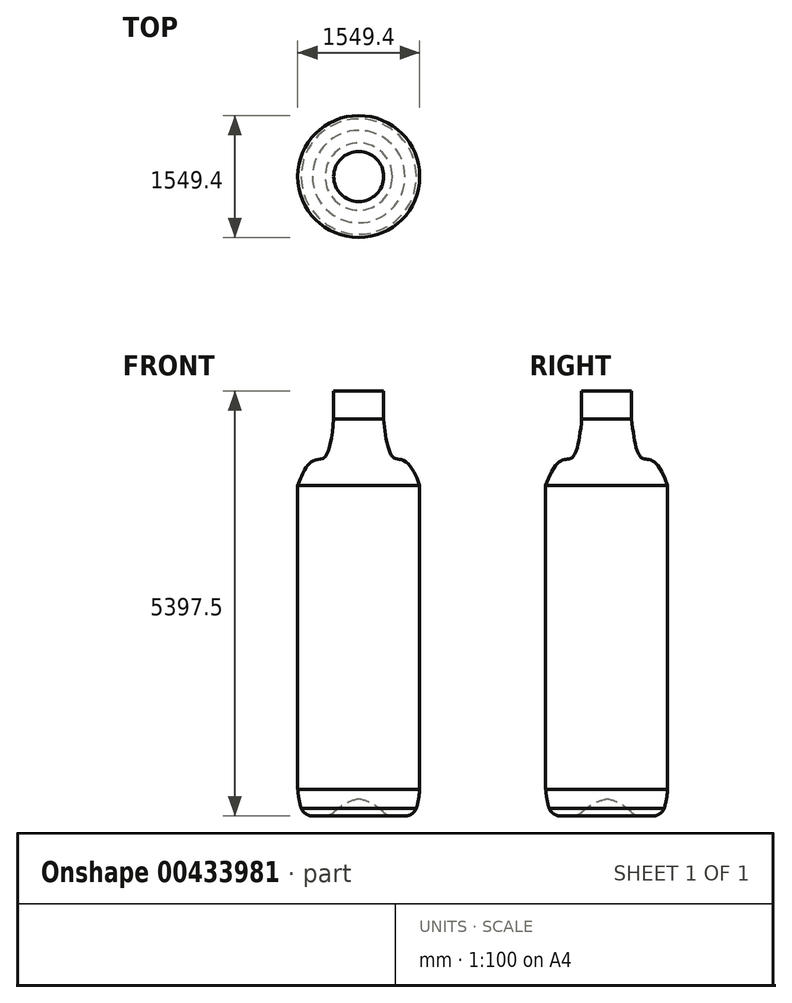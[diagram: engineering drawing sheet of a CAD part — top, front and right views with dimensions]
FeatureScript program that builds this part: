
annotation { "Feature Type Name" : "Feature", "Feature Type Description" : "" }
export const myFeature = defineFeature(function(context is Context, id is Id, definition is map)
    precondition{}
    {
        {
            var Q0;
            Q0=qCreatedBy(makeId("Front.planeOp"),FACE);
            var sketch = newSketch(context, id + "F0", { "sketchPlane" : qUnion([Q0])});
            skLineSegment(sketch, "E0", {"start": v(0, 0) * mm, "end": v(0, 355.6) * mm});
            skLineSegment(sketch, "E1", {"start": v(0, 355.6) * mm, "end": v(317.5, 355.6) * mm});
            skLineSegment(sketch, "E2", {"start": v(317.5, 355.6) * mm, "end": v(317.5, -4826) * mm});
            skLineSegment(sketch, "E3", {"start": v(2892.18, 355.6) * mm, "end": v(2892.18, -5041.9) * mm});
            skLineSegment(sketch, "E4", {"start": v(2892.18, -5041.9) * mm, "end": v(-1328.44, -5041.9) * mm});
            skArc(sketch, "E5", {"start": v(317.5, -4826) * mm, "mid": v(146.31, -4888.72) * mm, "end": v(0, -4997.49) * mm});
            skArc(sketch, "E6", {"start": v(-109.76, -5041.88) * mm, "mid": v(-50.4, -5030.78) * mm, "end": v(0, -4997.49) * mm});
            skArc(sketch, "E7", {"start": v(-414.32, -4943.65) * mm, "mid": v(-357.47, -5015.58) * mm, "end": v(-269.64, -5041.88) * mm});
            skArc(sketch, "E8", {"start": v(-457.2, -4702.39) * mm, "mid": v(-442.24, -4824.17) * mm, "end": v(-414.32, -4943.65) * mm});
            skLineSegment(sketch, "E9", {"start": v(-457.2, -4702.39) * mm, "end": v(-457.2, -846.82) * mm});
            skLineSegment(sketch, "E10.trimOffspring", {"start": v(-189.7, -5017.86) * mm, "end": v(-189.7, -3113.82) * mm});
            skLineSegment(sketch, "E11", {"start": v(-269.64, -5041.88) * mm, "end": v(-109.76, -5041.88) * mm});
            skFitSpline(sketch, "E12", {"points": [v(-457.2, -846.82) * mm, v(-121, -488.36) * mm, v(0, 0) * mm], "startDerivative": vector(883.63, 2567.96) * mm, "endDerivative": vector(100.32, 1087.1) * mm});
            skSolve(sketch);
        }
        {
            var Q0;
            Q0=makeQuery(id+"F0.imprint","IMPRINT",FACE,{"disambiguationData":[TD([[makeQuery(id+"F0.imprint","IMPRINT",EDGE,{"derivedFrom":sQuery(id+"F0.wireOp",EDGE,"E0")}),-1.0]])]});
            var Q1;
            Q1=sQuery(id+"F0.wireOp",EDGE,"E2");
            revolve(context, id + "F1", {"entities" : qUnion([Q0]), "axis" : qUnion([Q1]), "revolveType" : RevolveType.FULL});
        }
    });
